# Revit family: xTowel_Dispenser-Bobrick-ClassicSeries-3961-50
name_source: partatom
category: Specialty Equipment
revit_build: Autodesk Revit 2014 (Build: 20130308_1515(x64)
units: mm (PartAtom-declared; Revit-internal decimal feet)

## types (1)
- 3961-50
    ADA Compliant = Yes
    Assembly Code = E20
    Default Elevation = 44"
    Description = ClassicSeries® Convertible Universal Roll Towel Module
    Height = 18 1/4"
    Installation Type = Secured to cabinet.
    Length = 9 1/16"
    Manufacturer = Bobrick Washroom Equipment, Inc.
    Material = Stainless Steel-Bobrick-Type 304-Satin
    Model = 3961-50
    Price = Prices may vary. Please consult Manufacturer Representative for most up-to-date price list.
    Product Documentation Link = http://www.bobrick.com
    Product Page URL = http://www.bobrick.com
    Specification = Convertible universal touch-free roll towel module shall be Type 304 stainless steel with all-welded construction; exposed surfaces shall have satin finish. Door shall be secured to cabinet with a full-length stainless steel piano-hinge and equipped with a tumbler lock keyed like other Bobrick washroom accessories. Towel mechanism dispenses universal, 1-1/2" to 2" (38 to 51mm) diameter core, up to 8" (205mm) wide, 8" (205mm) diameter, non perforated, non-proprietary paper towel rolls. 800 ft (244mm) long. Touch-Free pull towel mechanism dispenses one 12" (300mm) length of towel per pull. User only touches the paper. Automatic transfer shall dispense stub roll up to 3-1/2" (90mm) diameter before new roll is dispensed. Equipped with paper towel feed wheel for use in filling the dispenser, or for user to advance paper should it become necessary to feed paper through dispenser. Paper towels are dispensed with pull force of less than 5 pounds (22.2 N) to comply with accessible design (including ADAAG in U.S.A.). Convertible Universal Touch.
    URL = http://www.bobrick.com
    Warranty Information = 1 Year Limited Warranty
    Width = 15 3/16"

## geometry (parser evidence)
native form markers: Sweep x2
no freeform markers — native parametric forms only
